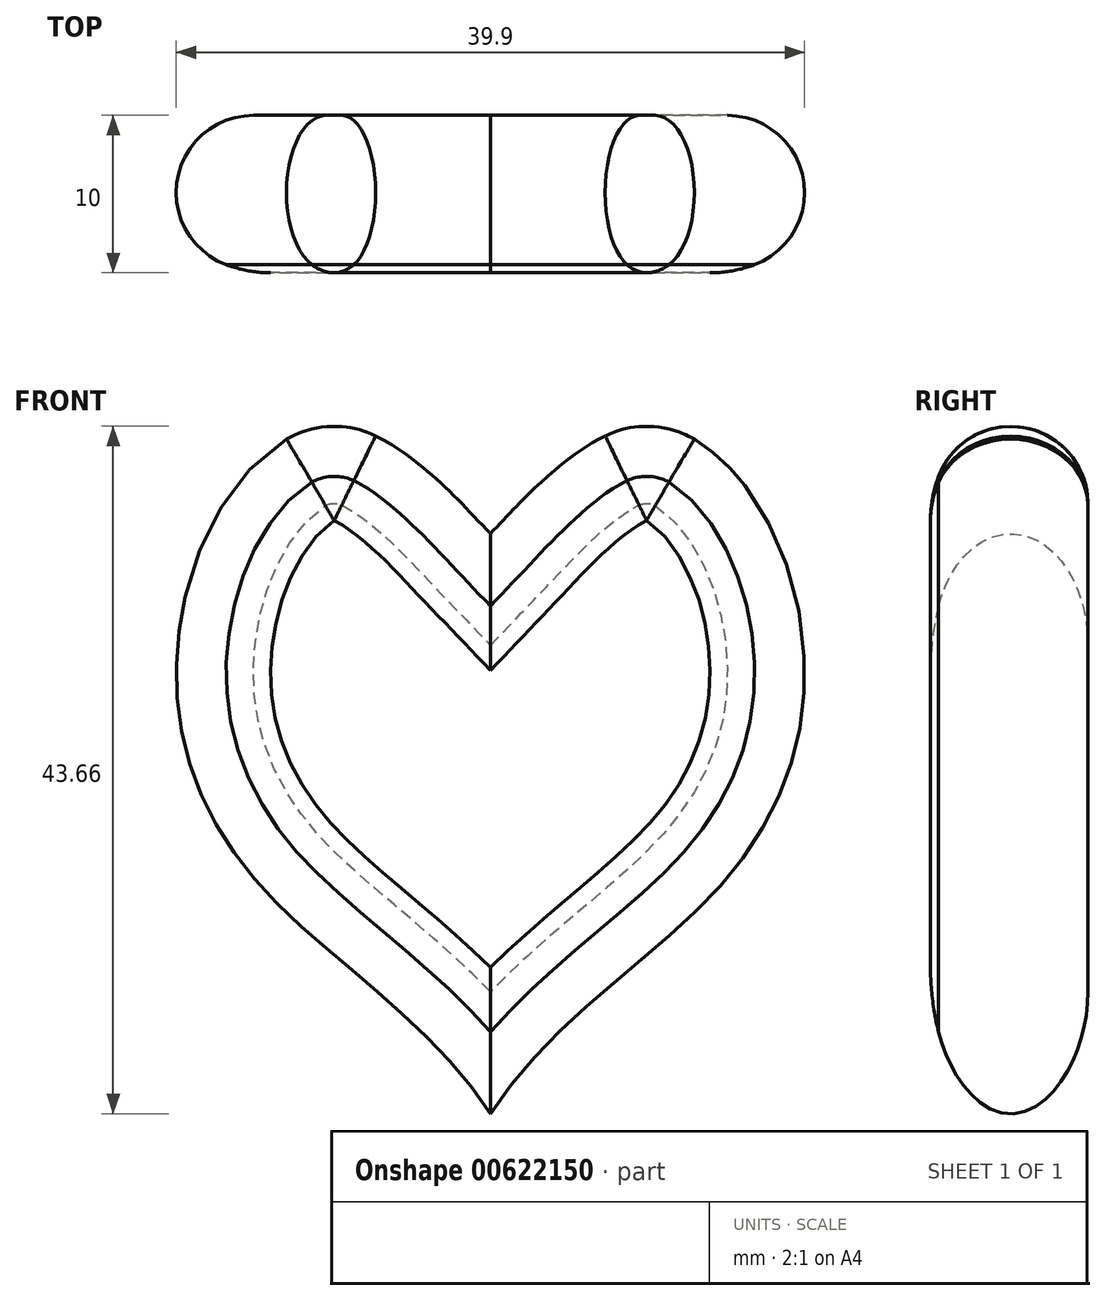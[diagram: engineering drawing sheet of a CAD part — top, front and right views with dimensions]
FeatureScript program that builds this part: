
annotation { "Feature Type Name" : "Feature", "Feature Type Description" : "" }
export const myFeature = defineFeature(function(context is Context, id is Id, definition is map)
    precondition{}
    {
        {
            var Q0;
            Q0=qCreatedBy(makeId("Front.planeOp"),FACE);
            var sketch = newSketch(context, id + "F0", { "sketchPlane" : qUnion([Q0])});
            skLineSegment(sketch, "E0", {"start": v(0, 0) * mm, "end": v(0, -50) * mm, "construction": true});
            skFitSpline(sketch, "E1", {"points": [v(0, -50) * mm, v(-15.41, -33.37) * mm, v(-21.9, -19.47) * mm, v(-18.32, -5.41) * mm, v(-9.5, 0) * mm, v(0, -6) * mm], "startDerivative": vector(-37.16, 89.05) * mm, "endDerivative": vector(44.13, -46.37) * mm});
            skFitSpline(sketch, "E2.MirrorCS", {"points": [v(0, -50) * mm, v(15.41, -33.37) * mm, v(21.9, -19.47) * mm, v(18.32, -5.41) * mm, v(9.5, 0) * mm, v(0, -6) * mm], "startDerivative": vector(37.16, 89.05) * mm, "endDerivative": vector(-44.13, -46.37) * mm});
            skSolve(sketch);
        }
        {
            var Q0;
            {var subQ1=sQuery(id+"F0.wireOp",EDGE,"E1");Q0=makeQuery(id+"F0.imprint","IMPRINT",FACE,{"disambiguationData":[TD([[makeQuery(id+"F0.imprint","IMPRINT",EDGE,{"derivedFrom":subQ1}),-1.0]])]});}
            var Q1;
            {var subQ0=sQuery(id+"F0.wireOp",EDGE,"E2.MirrorCS");Q1=makeQuery(id+"F0.imprint","IMPRINT",FACE,{"disambiguationData":[TD([[makeQuery(id+"F0.imprint","IMPRINT",EDGE,{"derivedFrom":subQ0}),1.0]])]});}
            extrude(context, id + "F1", {"entities" : qUnion([Q0, Q1]), "endBound" : BoundingType.SYMMETRIC, "depth" : 10 * mm, "offsetDistance" : 25 * mm});
        }
        {
            var Q0;
            Q0=makeQuery(id+"F1.opExtrude","CAP_FACE",FACE,{"disambiguationData":[OSD([sQuery(id+"F0.wireOp",EDGE,"E1"),sQuery(id+"F0.wireOp",EDGE,"E2.MirrorCS")])],"isStart":false});
            fillet(context, id + "F2", {"entities" : qUnion([Q0]), "radius" : 8 * mm, "tangentPropagation" : true, "allowEdgeOverflow" : false});
        }
        {
            var Q0;
            Q0=makeQuery(id+"F1.opExtrude","CAP_FACE",FACE,{"disambiguationData":[OSD([sQuery(id+"F0.wireOp",EDGE,"E1"),sQuery(id+"F0.wireOp",EDGE,"E2.MirrorCS")])],"isStart":true});
            fillet(context, id + "F3", {"entities" : qUnion([Q0]), "radius" : 4.9 * mm, "tangentPropagation" : true, "allowEdgeOverflow" : false});
        }
    });
